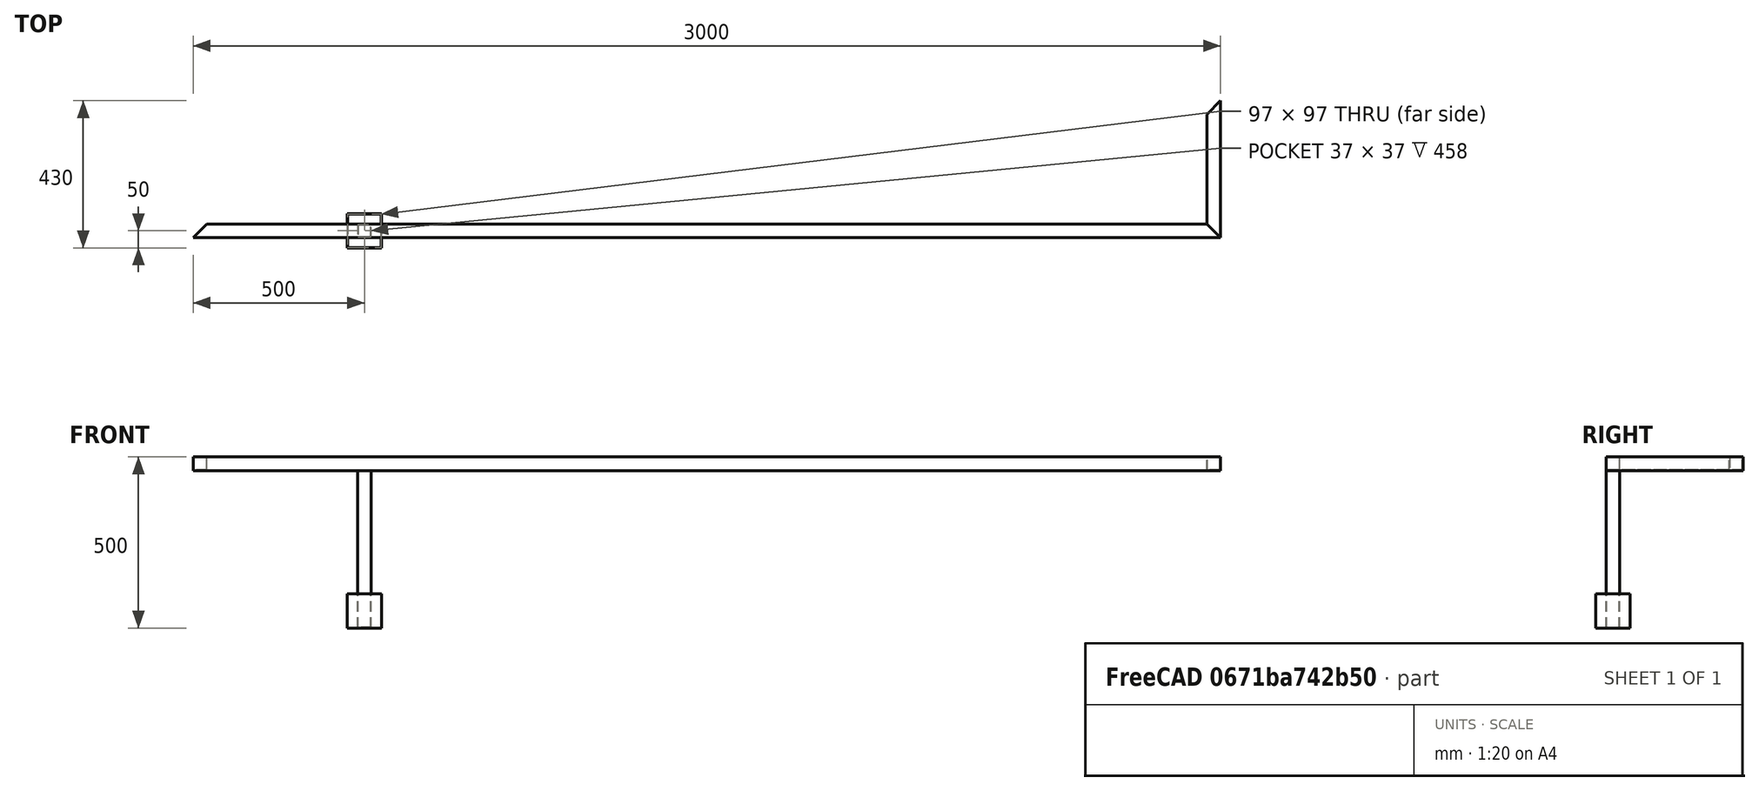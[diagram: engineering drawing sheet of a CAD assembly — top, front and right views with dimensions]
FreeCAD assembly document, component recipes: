
FREECAD ASSEMBLY — COMPONENT RECIPES ("podstavek")

This assembly document has 3 components, labeled P0..P2 below (a component is one placed body or linked part). 3 of them carry a construction recipe — the FreeCAD feature program that regenerates the part from scratch, quoted from this document or its linked companion documents; the rest are supplied as boundary geometry only. No exploded tour is included for this assembly.
COMPONENT P0 — recipe-attached ("frame_beam_1", modeled in this document).
Construction recipe (the document's own serialized feature program — sketch geometry with constraints, then the solid features built on it; lengths are millimeters unless a unit is written):

FEATURE [PartDesign::CoordinateSystem] LCS_0001
  AttacherType = Attacher::AttachEngine3D
  MapMode = 2
  Support = -> [X_Axis002]
FEATURE [Sketcher::SketchObject] Sketch
  FullyConstrained = true
  MapMode = 5
  Placement = pos=(0,0,0) rot=(0.57735,0.57735,0.57735;2.0944rad)
  Support = -> [YZ_Plane002]
  expr: Constraints[27] = Variables.depth / 2
  expr: Constraints[28] = Variables.height
  sketch-geometry (10):
    g0: LineSegment StartX=-160 StartY=460 StartZ=0 EndX=-160 EndY=500 EndZ=0
    g1: LineSegment StartX=-160 StartY=500 StartZ=0 EndX=-200 EndY=500 EndZ=0
    g2: LineSegment StartX=-200 StartY=500 StartZ=0 EndX=-200 EndY=460 EndZ=0
    g3: LineSegment StartX=-200 StartY=460 StartZ=0 EndX=-160 EndY=460 EndZ=0
    g4: Circle CenterX=-180 CenterY=480 CenterZ=0 NormalX=0 NormalY=0 NormalZ=1 AngleXU=0 Radius=28.2843
    g5: LineSegment StartX=-198.5 StartY=461.5 StartZ=0 EndX=-161.5 EndY=461.5 EndZ=0
    g6: LineSegment StartX=-161.5 StartY=461.5 StartZ=0 EndX=-161.5 EndY=498.5 EndZ=0
    g7: LineSegment StartX=-161.5 StartY=498.5 StartZ=0 EndX=-198.5 EndY=498.5 EndZ=0
    g8: LineSegment StartX=-198.5 StartY=498.5 StartZ=0 EndX=-198.5 EndY=461.5 EndZ=0
    g9: Circle CenterX=-180 CenterY=480 CenterZ=0 NormalX=0 NormalY=0 NormalZ=1 AngleXU=0 Radius=26.163
  constraints (29):
    c: Coincident(g0,g1)
    c: Coincident(g1,g2)
    c: Coincident(g2,g3)
    c: Coincident(g3,g0)
    c: Equal(g0,g1)
    c: Equal(g0,g2)
    c: Equal(g0,g3)
    c: PointOnObject(g0,g4)
    c: PointOnObject(g1,g4)
    c: PointOnObject(g2,g4)
    c: PointOnObject(g3,g4)
    c: Coincident(g5,g6)
    c: Coincident(g6,g7)
    c: Coincident(g7,g8)
    c: Coincident(g8,g5)
    c: Equal(g5,g6)
    c: Equal(g5,g7)
    c: Equal(g5,g8)
    c: PointOnObject(g5,g9)
    c: PointOnObject(g6,g9)
    c: PointOnObject(g7,g9)
    c: PointOnObject(g8,g9)
    c: Coincident(g9,g4)
    c: Horizontal(g3)
    c: Horizontal(g5)
    c: DistanceY(g0,g5) = 1.5  's'
    c: DistanceY(g0,g0) = 40
    c: DistanceX(g2,g-1) = 200
    c: DistanceY(g-1,g1) = 500
FEATURE [PartDesign::Pad] Pad
  Direction = (1,1,1)
  Length = 3000
  Length2 = 100
  Midplane = true
  Placement = pos=(0,0,0) rot=(0.57735,0.57735,0.57735;2.0944rad)
  Profile = -> Sketch
  Type = 0
  expr: Length = Variables.length
FEATURE [Sketcher::SketchObject] Sketch001
  ExternalGeometry = -> [Pad]
  FullyConstrained = true
  MapMode = 5
  Support = -> [XY_Plane002]
  sketch-geometry (6):
    g0: LineSegment StartX=-1500 StartY=-200 StartZ=0 EndX=-1460 EndY=-160 EndZ=0
    g1: LineSegment StartX=-1460 StartY=-160 StartZ=0 EndX=-1500 EndY=-160 EndZ=0
    g2: LineSegment StartX=-1500 StartY=-160 StartZ=0 EndX=-1500 EndY=-200 EndZ=0
    g3: LineSegment StartX=1500 StartY=-160 StartZ=0 EndX=1500 EndY=-200 EndZ=0
    g4: LineSegment StartX=1500 StartY=-160 StartZ=0 EndX=1460 EndY=-160 EndZ=0
    g5: LineSegment StartX=1460 StartY=-160 StartZ=0 EndX=1500 EndY=-200 EndZ=0
  constraints (14):
    c: Coincident(g0,g1)
    c: Horizontal(g1)
    c: Coincident(g1,g2)
    c: Equal(g2,g1)
    c: Coincident(g1,g-3)
    c: Coincident(g0,g2)
    c: Coincident(g0,g-3)
    c: Coincident(g3,g4)
    c: Horizontal(g4)
    c: Coincident(g4,g5)
    c: Coincident(g5,g3)
    c: Equal(g3,g4)
    c: Coincident(g3,g-4)
    c: Coincident(g3,g-4)
FEATURE [PartDesign::Pocket] Pocket
  BaseFeature = -> Pad
  Length = 5
  Length2 = 100
  Placement = pos=(0,0,0) rot=(0.57735,0.57735,0.57735;2.0944rad)
  Profile = -> Sketch001
  Reversed = true
  Type = 1
FEATURE [PartDesign::Body] Body
  Group = -> [LCS_0001,Sketch,Pad,Sketch001,Pocket]
  Origin = -> Origin002
  Tip = -> Pocket
COMPONENT P1 — recipe-attached ("frame_beam_2", modeled in this document).
Construction recipe (the document's own serialized feature program — sketch geometry with constraints, then the solid features built on it; lengths are millimeters unless a unit is written):

FEATURE [PartDesign::CoordinateSystem] LCS_0003
  AttacherType = Attacher::AttachEngine3D
  MapMode = 2
  Support = -> [X_Axis004]
FEATURE [Sketcher::SketchObject] Sketch002
  FullyConstrained = true
  MapMode = 5
  Placement = pos=(0,0,0) rot=(1,0,0;1.5708rad)
  Support = -> [XZ_Plane004]
  expr: Constraints[25] = Variables.beam_thickness
  expr: Constraints[28] = Variables.length / 2
  expr: Constraints[26] = Variables.beam_width
  expr: Constraints[27] = Variables.height
  sketch-geometry (10):
    g0: LineSegment StartX=1500 StartY=500 StartZ=0 EndX=1460 EndY=500 EndZ=0
    g1: LineSegment StartX=1460 StartY=500 StartZ=0 EndX=1460 EndY=460 EndZ=0
    g2: LineSegment StartX=1460 StartY=460 StartZ=0 EndX=1500 EndY=460 EndZ=0
    g3: LineSegment StartX=1500 StartY=460 StartZ=0 EndX=1500 EndY=500 EndZ=0
    g4: Circle CenterX=1480 CenterY=480 CenterZ=0 NormalX=0 NormalY=0 NormalZ=1 AngleXU=0 Radius=28.2843
    g5: LineSegment StartX=1498.5 StartY=498.5 StartZ=0 EndX=1461.5 EndY=498.5 EndZ=0
    g6: LineSegment StartX=1461.5 StartY=498.5 StartZ=0 EndX=1461.5 EndY=461.5 EndZ=0
    g7: LineSegment StartX=1461.5 StartY=461.5 StartZ=0 EndX=1498.5 EndY=461.5 EndZ=0
    g8: LineSegment StartX=1498.5 StartY=461.5 StartZ=0 EndX=1498.5 EndY=498.5 EndZ=0
    g9: Circle CenterX=1480 CenterY=480 CenterZ=0 NormalX=0 NormalY=0 NormalZ=1 AngleXU=0 Radius=26.163
  constraints (29):
    c: Coincident(g0,g1)
    c: Coincident(g1,g2)
    c: Coincident(g2,g3)
    c: Coincident(g3,g0)
    c: Equal(g0,g1)
    c: Equal(g0,g2)
    c: Equal(g0,g3)
    c: PointOnObject(g0,g4)
    c: PointOnObject(g1,g4)
    c: PointOnObject(g2,g4)
    c: PointOnObject(g3,g4)
    c: Coincident(g5,g6)
    c: Coincident(g6,g7)
    c: Coincident(g7,g8)
    c: Coincident(g8,g5)
    c: Equal(g5,g6)
    c: Equal(g5,g7)
    c: Equal(g5,g8)
    c: PointOnObject(g5,g9)
    c: PointOnObject(g6,g9)
    c: PointOnObject(g7,g9)
    c: PointOnObject(g8,g9)
    c: Coincident(g9,g4)
    c: Horizontal(g7)
    c: Horizontal(g2)
    c: DistanceY(g2,g7) = 1.5
    c: DistanceY(g3,g3) = 40
    c: DistanceY(g-1,g0) = 500
    c: DistanceX(g-1,g2) = 1500
FEATURE [PartDesign::Pad] Pad001
  Direction = (1,1,1)
  Length = 400
  Length2 = 100
  Midplane = true
  Placement = pos=(0,0,0) rot=(1,0,0;1.5708rad)
  Profile = -> Sketch002
  Type = 0
  expr: Length = Variables.depth
FEATURE [Sketcher::SketchObject] Sketch003
  ExternalGeometry = -> [Pad001]
  FullyConstrained = true
  MapMode = 5
  Support = -> [XY_Plane004]
  sketch-geometry (6):
    g0: LineSegment StartX=1460 StartY=200 StartZ=0 EndX=1500 EndY=200 EndZ=0
    g1: LineSegment StartX=1500 StartY=200 StartZ=0 EndX=1460 EndY=160 EndZ=0
    g2: LineSegment StartX=1460 StartY=160 StartZ=0 EndX=1460 EndY=200 EndZ=0
    g3: LineSegment StartX=1460 StartY=-200 StartZ=0 EndX=1460 EndY=-160 EndZ=0
    g4: LineSegment StartX=1460 StartY=-160 StartZ=0 EndX=1500 EndY=-200 EndZ=0
    g5: LineSegment StartX=1500 StartY=-200 StartZ=0 EndX=1460 EndY=-200 EndZ=0
  constraints (14):
    c: Coincident(g0,g1)
    c: Coincident(g1,g2)
    c: Coincident(g2,g0)
    c: Vertical(g3)
    c: Coincident(g3,g4)
    c: Coincident(g4,g5)
    c: Coincident(g5,g3)
    c: Vertical(g2)
    c: Equal(g2,g0)
    c: Equal(g3,g5)
    c: Coincident(g3,g-4)
    c: Coincident(g4,g-4)
    c: Coincident(g0,g-3)
    c: Coincident(g0,g-3)
FEATURE [PartDesign::Pocket] Pocket001
  BaseFeature = -> Pad001
  Length = 5
  Length2 = 100
  Placement = pos=(0,0,0) rot=(1,0,0;1.5708rad)
  Profile = -> Sketch003
  Reversed = true
  Type = 1
FEATURE [PartDesign::Body] Body_2
  Group = -> [LCS_0003,Sketch002,Pad001,Sketch003,Pocket001]
  Origin = -> Origin004
  Tip = -> Pocket001
COMPONENT P2 — recipe-attached ("leg", modeled in this document).
Construction recipe (the document's own serialized feature program — sketch geometry with constraints, then the solid features built on it; lengths are millimeters unless a unit is written):

FEATURE [PartDesign::CoordinateSystem] LCS_0005
  AttacherType = Attacher::AttachEngine3D
  MapMode = 2
  Support = -> [X_Axis006]
FEATURE [Sketcher::SketchObject] Sketch004
  FullyConstrained = true
  MapMode = 5
  Support = -> [XY_Plane006]
  expr: Constraints[14] = (Variables.depth - Variables.beam_width) / 2
  expr: Constraints[13] = Variables.length / 3
  sketch-geometry (5):
    g0: LineSegment StartX=-950 StartY=-130 StartZ=0 EndX=-1050 EndY=-130 EndZ=0
    g1: LineSegment StartX=-1050 StartY=-130 StartZ=0 EndX=-1050 EndY=-230 EndZ=0
    g2: LineSegment StartX=-1050 StartY=-230 StartZ=0 EndX=-950 EndY=-230 EndZ=0
    g3: LineSegment StartX=-950 StartY=-230 StartZ=0 EndX=-950 EndY=-130 EndZ=0
    g4: Circle CenterX=-1000 CenterY=-180 CenterZ=0 NormalX=0 NormalY=0 NormalZ=1 AngleXU=0 Radius=70.7107
  constraints (15):
    c: Coincident(g0,g1)
    c: Coincident(g1,g2)
    c: Coincident(g2,g3)
    c: Coincident(g3,g0)
    c: Equal(g0,g1)
    c: Equal(g0,g2)
    c: Equal(g0,g3)
    c: PointOnObject(g0,g4)
    c: PointOnObject(g1,g4)
    c: PointOnObject(g2,g4)
    c: PointOnObject(g3,g4)
    c: Horizontal(g2)
    c: DistanceX(g2,g2) = 100
    c: DistanceX(g4,g-1) = 1000
    c: DistanceY(g4,g-1) = 180
FEATURE [PartDesign::Pad] Pad002
  Direction = (1,1,1)
  Length = 2
  Length2 = 100
  Profile = -> Sketch004
  Type = 0
FEATURE [Sketcher::SketchObject] Sketch005
  ExternalGeometry = -> [Pad002]
  FullyConstrained = true
  MapMode = 5
  Placement = pos=(0,0,2) rot=(0,0,1;0rad)
  Support = -> [Pad002,XY_Plane]
  expr: Constraints[30] = Variables.beam_thickness
  expr: Constraints[29] = Variables.beam_width
  sketch-geometry (11):
    g0: LineSegment StartX=-980 StartY=-160 StartZ=0 EndX=-1020 EndY=-160 EndZ=0
    g1: LineSegment StartX=-1020 StartY=-160 StartZ=0 EndX=-1020 EndY=-200 EndZ=0
    g2: LineSegment StartX=-1020 StartY=-200 StartZ=0 EndX=-980 EndY=-200 EndZ=0
    g3: LineSegment StartX=-980 StartY=-200 StartZ=0 EndX=-980 EndY=-160 EndZ=0
    g4: Circle CenterX=-1000 CenterY=-180 CenterZ=0 NormalX=0 NormalY=0 NormalZ=1 AngleXU=0 Radius=28.2843
    g5: LineSegment StartX=-981.5 StartY=-161.5 StartZ=0 EndX=-1018.5 EndY=-161.5 EndZ=0
    g6: LineSegment StartX=-1018.5 StartY=-161.5 StartZ=0 EndX=-1018.5 EndY=-198.5 EndZ=0
    g7: LineSegment StartX=-1018.5 StartY=-198.5 StartZ=0 EndX=-981.5 EndY=-198.5 EndZ=0
    g8: LineSegment StartX=-981.5 StartY=-198.5 StartZ=0 EndX=-981.5 EndY=-161.5 EndZ=0
    g9: Circle CenterX=-1000 CenterY=-180 CenterZ=0 NormalX=0 NormalY=0 NormalZ=1 AngleXU=0 Radius=26.163
    g10: Circle CenterX=-1000 CenterY=-180 CenterZ=0 NormalX=0 NormalY=0 NormalZ=1 AngleXU=0 Radius=70.7107
  constraints (31):
    c: Coincident(g0,g1)
    c: Coincident(g1,g2)
    c: Coincident(g2,g3)
    c: Coincident(g3,g0)
    c: Equal(g0,g1)
    c: Equal(g0,g2)
    c: Equal(g0,g3)
    c: PointOnObject(g0,g4)
    c: PointOnObject(g1,g4)
    c: PointOnObject(g2,g4)
    c: PointOnObject(g3,g4)
    c: Coincident(g5,g6)
    c: Coincident(g6,g7)
    c: Coincident(g7,g8)
    c: Coincident(g8,g5)
    c: Equal(g5,g6)
    c: Equal(g5,g7)
    c: Equal(g5,g8)
    c: PointOnObject(g5,g9)
    c: PointOnObject(g6,g9)
    c: PointOnObject(g7,g9)
    c: PointOnObject(g8,g9)
    c: Coincident(g9,g4)
    c: Coincident(g10,g4)
    c: PointOnObject(g-3,g10)
    c: PointOnObject(g-4,g10)
    c: PointOnObject(g-4,g10)
    c: Horizontal(g7)
    c: Horizontal(g2)
    c: DistanceY(g3,g3) = 40
    c: DistanceY(g2,g7) = 1.5
FEATURE [PartDesign::Pad] Pad003
  BaseFeature = -> Pad002
  Direction = (1,1,1)
  Length = 458
  Length2 = 100
  Profile = -> Sketch005
  Type = 0
  expr: Length = Variables.height - Variables.beam_width - 2
FEATURE [Sketcher::SketchObject] Sketch006
  ExternalGeometry = -> [Pad003]
  FullyConstrained = true
  MapMode = 5
  Support = -> [XY_Plane006]
  expr: Constraints[16] = Variables.beam_thickness
  sketch-geometry (10):
    g0: LineSegment StartX=-951.5 StartY=-131.5 StartZ=0 EndX=-1048.5 EndY=-131.5 EndZ=0
    g1: LineSegment StartX=-1048.5 StartY=-131.5 StartZ=0 EndX=-1048.5 EndY=-228.5 EndZ=0
    g2: LineSegment StartX=-1048.5 StartY=-228.5 StartZ=0 EndX=-951.5 EndY=-228.5 EndZ=0
    g3: LineSegment StartX=-951.5 StartY=-228.5 StartZ=0 EndX=-951.5 EndY=-131.5 EndZ=0
    g4: Circle CenterX=-1000 CenterY=-180 CenterZ=0 NormalX=0 NormalY=0 NormalZ=1 AngleXU=0 Radius=68.5894
    g5: Circle CenterX=-1000 CenterY=-180 CenterZ=0 NormalX=0 NormalY=0 NormalZ=1 AngleXU=0 Radius=70.7107
    g6: LineSegment StartX=-1050 StartY=-130 StartZ=0 EndX=-950 EndY=-130 EndZ=0
    g7: LineSegment StartX=-950 StartY=-130 StartZ=0 EndX=-950 EndY=-230 EndZ=0
    g8: LineSegment StartX=-950 StartY=-230 StartZ=0 EndX=-1050 EndY=-230 EndZ=0
    g9: LineSegment StartX=-1050 StartY=-130 StartZ=0 EndX=-1050 EndY=-230 EndZ=0
  constraints (25):
    c: Coincident(g0,g1)
    c: Coincident(g1,g2)
    c: Coincident(g2,g3)
    c: Coincident(g3,g0)
    c: Equal(g0,g1)
    c: Equal(g0,g2)
    c: Equal(g0,g3)
    c: PointOnObject(g0,g4)
    c: PointOnObject(g1,g4)
    c: PointOnObject(g2,g4)
    c: PointOnObject(g3,g4)
    c: Horizontal(g2)
    c: Coincident(g5,g4)
    c: PointOnObject(g-5,g5)
    c: PointOnObject(g-4,g5)
    c: PointOnObject(g-6,g5)
    c: DistanceY(g0,g-5) = 1.5
    c: Coincident(g-4,g6)
    c: Coincident(g6,g-5)
    c: Coincident(g6,g7)
    c: Coincident(g7,g-6)
    c: Coincident(g7,g8)
    c: Coincident(g8,g-6)
    c: Coincident(g9,g6)
    c: Coincident(g9,g8)
FEATURE [PartDesign::Pad] Pad004
  BaseFeature = -> Pad003
  Direction = (1,1,1)
  Length = 100
  Length2 = 100
  Profile = -> Sketch006
  Type = 0
FEATURE [PartDesign::Body] Body_3
  Group = -> [LCS_0005,Sketch004,Pad002,Sketch005,Pad003,Sketch006,Pad004]
  Origin = -> Origin006
  Tip = -> Pad004
PROVENANCE & LICENSES
A FreeCAD (.FCStd) document from a public repository crawl; recipes are the document's own serialized feature recipes (and, for linked parts, companion documents' recipes).
License: apache-2.0.
